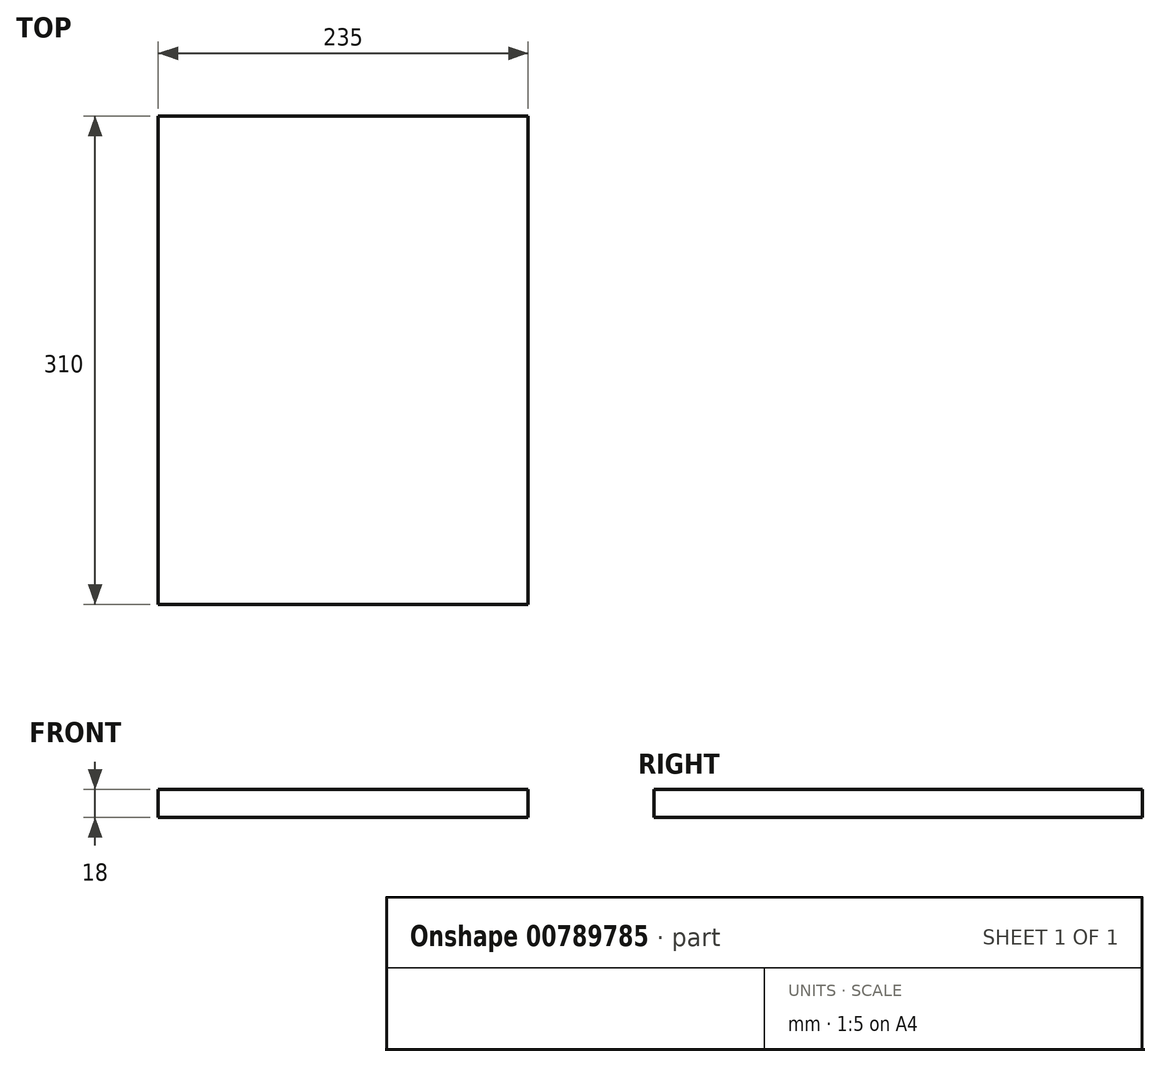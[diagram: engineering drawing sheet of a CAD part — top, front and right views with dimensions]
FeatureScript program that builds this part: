
annotation { "Feature Type Name" : "Feature", "Feature Type Description" : "" }
export const myFeature = defineFeature(function(context is Context, id is Id, definition is map)
    precondition{}
    {
        {
            var Q0;
            Q0=qCreatedBy(makeId("Top.planeOp"),FACE);
            var sketch = newSketch(context, id + "F0", { "sketchPlane" : qUnion([Q0])});
            skLineSegment(sketch, "E0.bottom", {"start": v(-122.49, 149.66) * mm, "end": v(112.51, 149.66) * mm});
            skLineSegment(sketch, "E0.top", {"start": v(-122.49, -160.34) * mm, "end": v(112.51, -160.34) * mm});
            skLineSegment(sketch, "E0.left", {"start": v(-122.49, 149.66) * mm, "end": v(-122.49, -160.34) * mm});
            skLineSegment(sketch, "E0.right", {"start": v(112.51, 149.66) * mm, "end": v(112.51, -160.34) * mm});
            skSolve(sketch);
        }
        {
            var Q0;
            Q0 = qSketchRegion(id + "F0", true);
            extrude(context, id + "F1", {"entities" : qUnion([Q0]), "depth" : 18 * mm, "offsetDistance" : 25 * mm});
        }
    });
